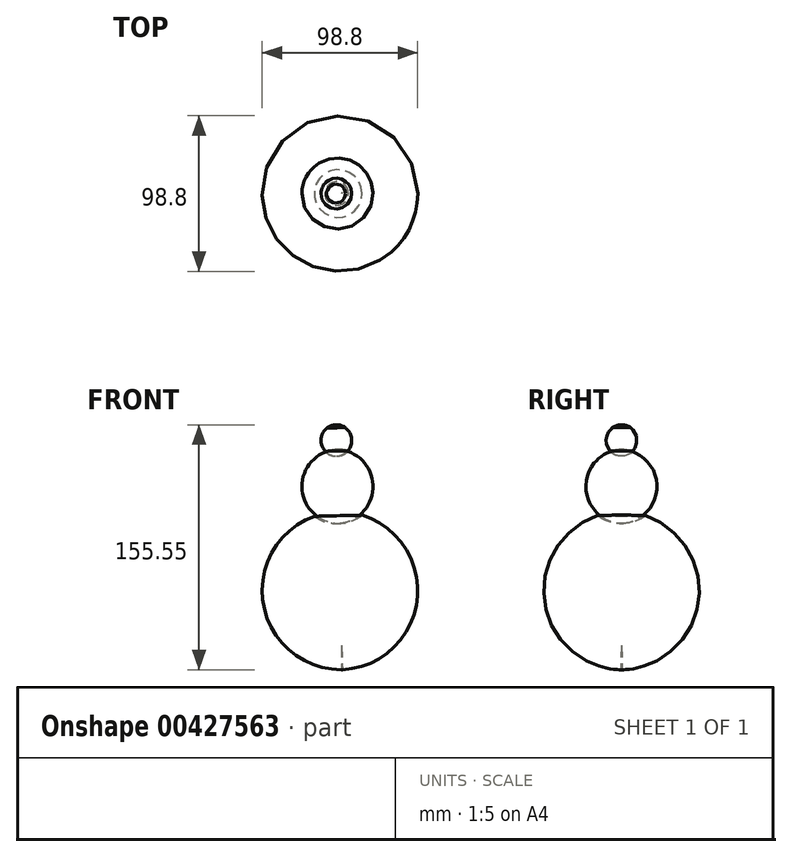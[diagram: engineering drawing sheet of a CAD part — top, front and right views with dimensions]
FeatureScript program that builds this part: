
annotation { "Feature Type Name" : "Feature", "Feature Type Description" : "" }
export const myFeature = defineFeature(function(context is Context, id is Id, definition is map)
    precondition{}
    {
        {
            var Q0;
            Q0=qCreatedBy(makeId("Front.planeOp"),FACE);
            var sketch = newSketch(context, id + "F0", { "sketchPlane" : qUnion([Q0])});
            skArc(sketch, "E0", {"start": v(-55.95, 3.3) * mm, "mid": v(-88.28, -52.62) * mm, "end": v(-38.8, -94.15) * mm});
            skArc(sketch, "E1.trimOffspring", {"start": v(-49.34, 44.59) * mm, "mid": v(-65.28, 25.97) * mm, "end": v(-55.95, 3.3) * mm});
            skLineSegment(sketch, "E2", {"start": v(-48.1, 59.4) * mm, "end": v(-42.11, 59.4) * mm});
            skArc(sketch, "E3.trimOffspring", {"start": v(-48.1, 59.4) * mm, "mid": v(-52.03, 52.27) * mm, "end": v(-49.34, 44.59) * mm});
            skLineSegment(sketch, "E4", {"start": v(-42.11, 59.4) * mm, "end": v(-38.8, -78.8) * mm});
            skLineSegment(sketch, "E5", {"start": v(-38.8, -78.8) * mm, "end": v(-38.8, -94.15) * mm});
            skPoint(sketch, "E6.orphan", {"position": v(-36.13, 59.4) * mm});
            skSolve(sketch);
        }
        {
            var Q0;
            Q0 = qSketchRegion(id + "F0", true);
            var Q1;
            Q1=sQuery(id+"F0.wireOp",EDGE,"E4");
            revolve(context, id + "F1", {"entities" : qUnion([Q0]), "axis" : qUnion([Q1]), "revolveType" : RevolveType.FULL});
        }
    });
